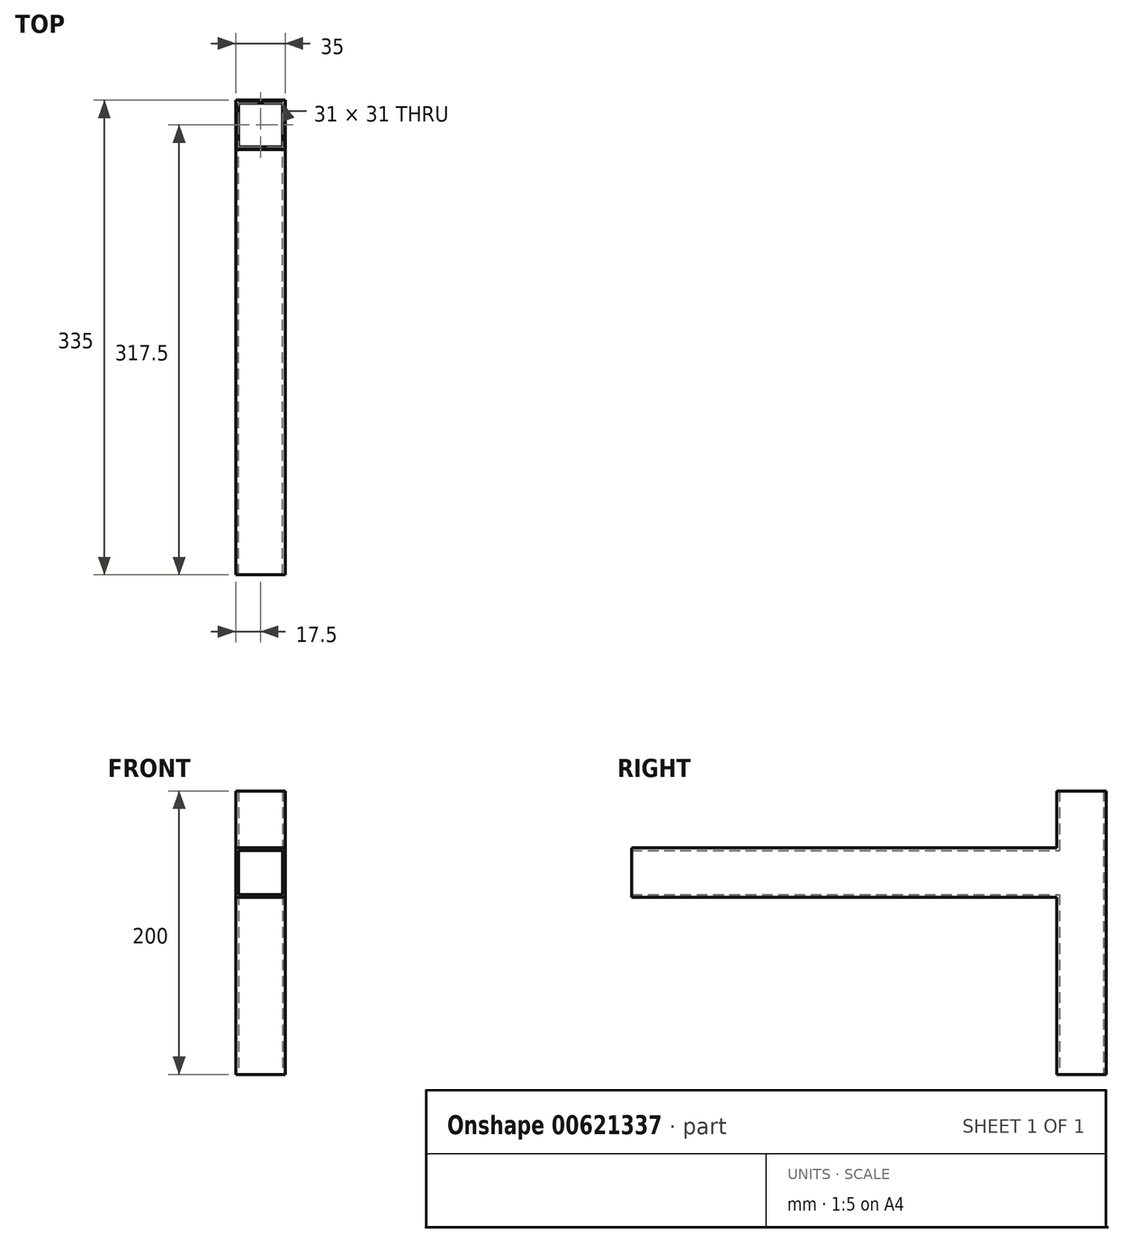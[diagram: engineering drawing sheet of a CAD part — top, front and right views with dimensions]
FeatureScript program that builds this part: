
annotation { "Feature Type Name" : "Feature", "Feature Type Description" : "" }
export const myFeature = defineFeature(function(context is Context, id is Id, definition is map)
    precondition{}
    {
        {
            var Q0;
            Q0=qCreatedBy(makeId("Right.planeOp"),FACE);
            var sketch = newSketch(context, id + "F0", { "sketchPlane" : qUnion([Q0])});
            skLineSegment(sketch, "E0.bottom", {"start": v(0, 0) * mm, "end": v(300, 0) * mm});
            skLineSegment(sketch, "E0.top", {"start": v(0, -35) * mm, "end": v(300, -35) * mm});
            skLineSegment(sketch, "E0.left", {"start": v(0, -35) * mm, "end": v(0, 0) * mm});
            skLineSegment(sketch, "E0.right", {"start": v(300, -35) * mm, "end": v(300, 0) * mm});
            skPoint(sketch, "E1.firstSnap0", {"position": v(300, -17.5) * mm});
            skLineSegment(sketch, "E1.bottom", {"start": v(300, 40) * mm, "end": v(335, 40) * mm});
            skLineSegment(sketch, "E1.top", {"start": v(300, -160) * mm, "end": v(335, -160) * mm});
            skLineSegment(sketch, "E1.left", {"start": v(300, 40) * mm, "end": v(300, -160) * mm});
            skLineSegment(sketch, "E1.right", {"start": v(335, 40) * mm, "end": v(335, -160) * mm});
            skLineSegment(sketch, "E2", {"start": v(300, 40) * mm, "end": v(300, -35) * mm});
            skLineSegment(sketch, "E3", {"start": v(300, 0) * mm, "end": v(300, -160) * mm});
            skSolve(sketch);
        }
        {
            var Q0;
            Q0=makeQuery(id+"F0.imprint","IMPRINT",FACE,{"disambiguationData":[TD([[makeQuery(id+"F0.imprint","IMPRINT",EDGE,{"derivedFrom":sQuery(id+"F0.wireOp",EDGE,"E0.bottom")}),-1.0]])]});
            var Q1;
            {var subQ1=sQuery(id+"F0.wireOp",EDGE,"E0.right");Q1=makeQuery(id+"F0.imprint","IMPRINT",FACE,{"disambiguationData":[TD([[makeQuery(id+"F0.imprint","IMPRINT",EDGE,{"derivedFrom":subQ1}),-1.0]])]});}
            extrude(context, id + "F1", {"entities" : qUnion([Q0, Q1]), "depth" : 35 * mm, "offsetDistance" : 25 * mm});
        }
        {
            var Q0;
            Q0=makeQuery(id+"F1.opExtrude","SWEPT_FACE",FACE,{"disambiguationData":[OSD([sQuery(id+"F0.wireOp",EDGE,"E1.bottom")])]});
            var Q1;
            Q1=makeQuery(id+"F1.opExtrude","SWEPT_FACE",FACE,{"disambiguationData":[OSD([sQuery(id+"F0.wireOp",EDGE,"E0.left")])]});
            var Q2;
            Q2=makeQuery(id+"F1.opExtrude","SWEPT_FACE",FACE,{"disambiguationData":[OSD([sQuery(id+"F0.wireOp",EDGE,"E1.top")])]});
            shell(context, id + "F2", {"entities" : qUnion([Q0, Q1, Q2]), "thickness" : 2 * mm});
        }
    });
